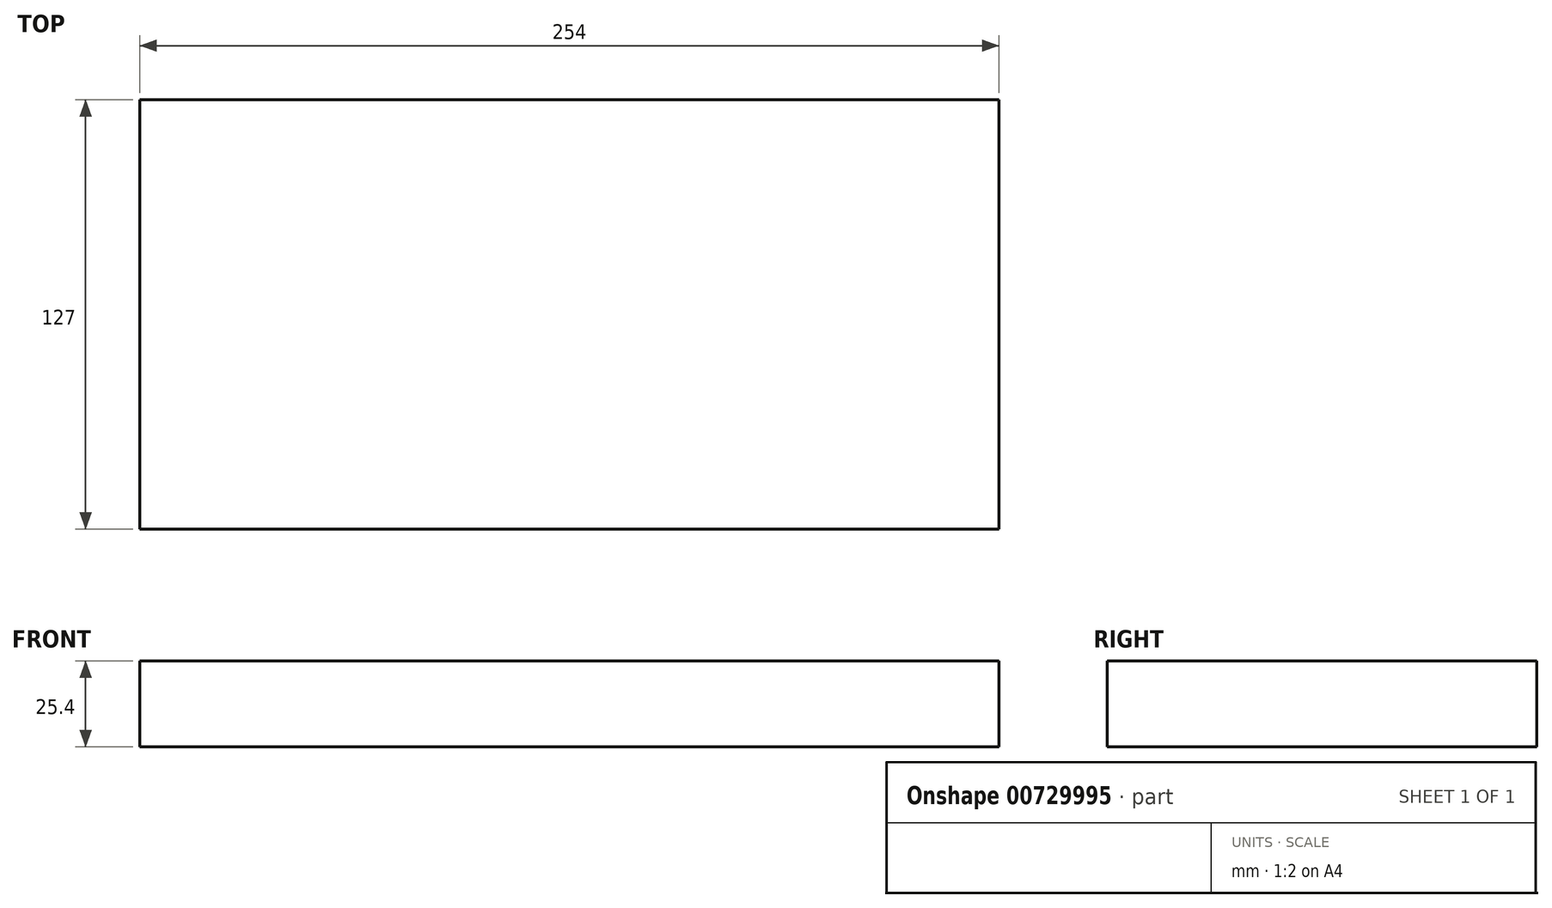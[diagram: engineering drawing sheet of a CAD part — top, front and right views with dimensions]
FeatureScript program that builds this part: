
annotation { "Feature Type Name" : "Feature", "Feature Type Description" : "" }
export const myFeature = defineFeature(function(context is Context, id is Id, definition is map)
    precondition{}
    {
        {
            var Q0;
            Q0=qCreatedBy(makeId("Top.planeOp"),FACE);
            var sketch = newSketch(context, id + "F0", { "sketchPlane" : qUnion([Q0])});
            skLineSegment(sketch, "E0.bottom", {"start": v(-127.6, -56.7) * mm, "end": v(126.4, -56.7) * mm});
            skLineSegment(sketch, "E0.top", {"start": v(-127.6, 70.3) * mm, "end": v(126.4, 70.3) * mm});
            skLineSegment(sketch, "E0.left", {"start": v(-127.6, -56.7) * mm, "end": v(-127.6, 70.3) * mm});
            skLineSegment(sketch, "E0.right", {"start": v(126.4, -56.7) * mm, "end": v(126.4, 70.3) * mm});
            skSolve(sketch);
        }
        {
            var Q0;
            Q0=makeQuery(id+"F0.imprint","IMPRINT",FACE,{"disambiguationData":[TD([[makeQuery(id+"F0.imprint","IMPRINT",EDGE,{"derivedFrom":sQuery(id+"F0.wireOp",EDGE,"E0.bottom")}),1.0]])]});
            extrude(context, id + "F1", {"entities" : qUnion([Q0]), "depth" : 25.4 * mm, "offsetDistance" : 25.4 * mm});
        }
    });
